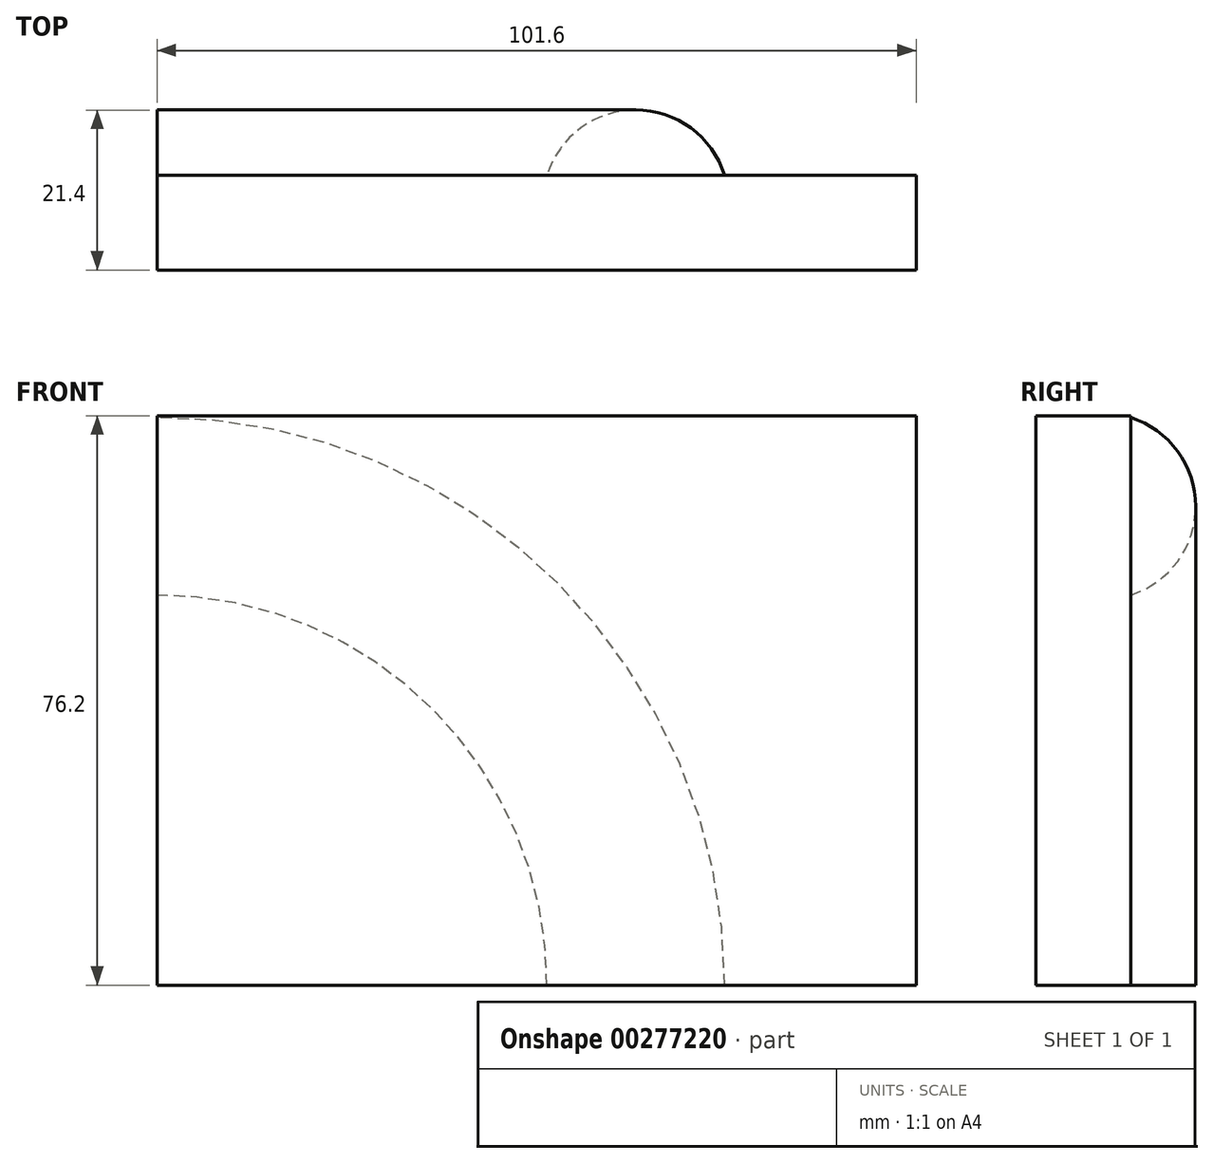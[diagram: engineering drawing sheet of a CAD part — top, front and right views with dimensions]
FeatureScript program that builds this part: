
annotation { "Feature Type Name" : "Feature", "Feature Type Description" : "" }
export const myFeature = defineFeature(function(context is Context, id is Id, definition is map)
    precondition{}
    {
        {
            var Q0;
            Q0=qCreatedBy(makeId("Front.planeOp"),FACE);
            var sketch = newSketch(context, id + "F0", { "sketchPlane" : qUnion([Q0])});
            skLineSegment(sketch, "E0.bottom", {"start": v(0, 0) * mm, "end": v(101.6, 0) * mm});
            skLineSegment(sketch, "E0.top", {"start": v(0, 76.2) * mm, "end": v(101.6, 76.2) * mm});
            skLineSegment(sketch, "E0.left", {"start": v(0, 0) * mm, "end": v(0, 76.2) * mm});
            skLineSegment(sketch, "E0.right", {"start": v(101.6, 0) * mm, "end": v(101.6, 76.2) * mm});
            skArc(sketch, "E1", {"start": v(0, 76.2) * mm, "mid": v(53.88, 53.88) * mm, "end": v(76.2, 0) * mm});
            skSolve(sketch);
        }
        {
            var Q0;
            Q0=qCreatedBy(makeId("Top.planeOp"),FACE);
            var sketch = newSketch(context, id + "F1", { "sketchPlane" : qUnion([Q0])});
            skArc(sketch, "E2", {"start": v(75.96, 0) * mm, "mid": v(64.08, 8.7) * mm, "end": v(52.2, 0) * mm});
            skLineSegment(sketch, "E3", {"start": v(52.2, 0) * mm, "end": v(75.96, 0) * mm});
            skSolve(sketch);
        }
        {
            var Q0;
            Q0=makeQuery(id+"F1.imprint","IMPRINT",FACE,{"disambiguationData":[TD([[makeQuery(id+"F1.imprint","IMPRINT",EDGE,{"derivedFrom":sQuery(id+"F1.wireOp",EDGE,"E2")}),1.0]])]});
            var Q1;
            Q1=sQuery(id+"F0.wireOp",EDGE,"E1");
            sweep(context, id + "F2", {"profiles" : qUnion([Q0]), "path" : qUnion([Q1])});
        }
        {
            var Q0;
            Q0 = qSketchRegion(id + "F0", true);
            extrude(context, id + "F3", {"entities" : qUnion([Q0]), "operationType" : NewBodyOperationType.ADD, "depth" : 12.7 * mm});
        }
    });
